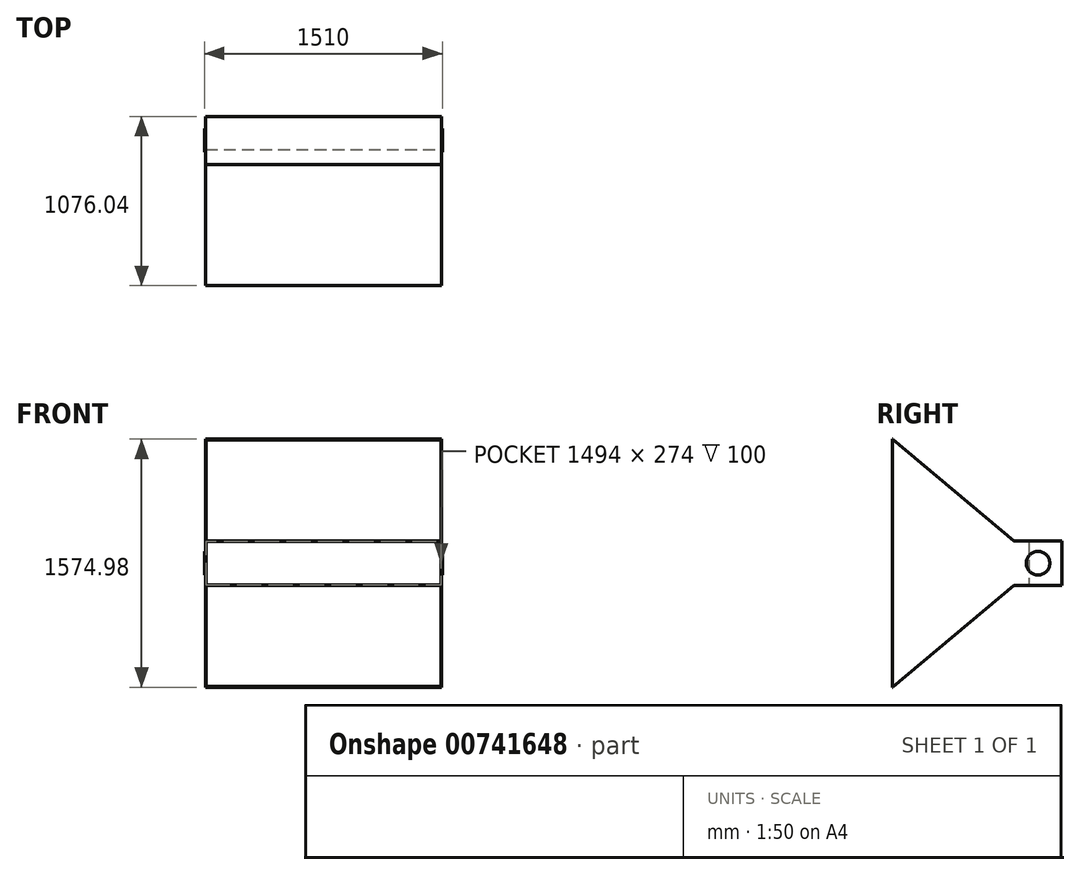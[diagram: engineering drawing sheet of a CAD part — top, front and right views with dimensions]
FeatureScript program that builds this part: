
annotation { "Feature Type Name" : "Feature", "Feature Type Description" : "" }
export const myFeature = defineFeature(function(context is Context, id is Id, definition is map)
    precondition{}
    {
        {
            var Q0;
            Q0=qCreatedBy(makeId("Front.planeOp"),FACE);
            var sketch = newSketch(context, id + "F0", { "sketchPlane" : qUnion([Q0])});
            skLineSegment(sketch, "E0.bottom", {"start": v(-750, 140) * mm, "end": v(750, 140) * mm});
            skLineSegment(sketch, "E0.top", {"start": v(-750, -140) * mm, "end": v(750, -140) * mm});
            skLineSegment(sketch, "E0.left", {"start": v(-750, 140) * mm, "end": v(-750, -140) * mm});
            skLineSegment(sketch, "E0.right", {"start": v(750, 140) * mm, "end": v(750, -140) * mm});
            skPoint(sketch, "E0.middle", {"position": v(0, 0) * mm});
            skSolve(sketch);
        }
        {
            var Q0;
            Q0=qSketchRegion(id+"F0",true);
            extrude(context, id + "F1", {"entities" : qUnion([Q0]), "oppositeDirection" : true, "depth" : 210 * mm});
        }
        {
            var Q0;
            Q0=makeQuery(id+"F1.opExtrude","CAP_FACE",FACE,{"disambiguationData":[OSD([sQuery(id+"F0.wireOp",EDGE,"E0.bottom"),sQuery(id+"F0.wireOp",EDGE,"E0.top"),sQuery(id+"F0.wireOp",EDGE,"E0.left"),sQuery(id+"F0.wireOp",EDGE,"E0.right")])],"isStart":true});
            var sketch = newSketch(context, id + "F2", { "sketchPlane" : qUnion([Q0])});
            skLineSegment(sketch, "E1.bottom", {"start": v(-750, 140) * mm, "end": v(750, 140) * mm});
            skLineSegment(sketch, "E1.top", {"start": v(-750, -140) * mm, "end": v(750, -140) * mm});
            skLineSegment(sketch, "E1.left", {"start": v(-750, 140) * mm, "end": v(-750, -140) * mm});
            skLineSegment(sketch, "E1.right", {"start": v(750, 140) * mm, "end": v(750, -140) * mm});
            skPoint(sketch, "E1.middle", {"position": v(0, 0) * mm});
            skLineSegment(sketch, "E2.bottom", {"start": v(-747, 137) * mm, "end": v(747, 137) * mm});
            skLineSegment(sketch, "E2.top", {"start": v(-747, -137) * mm, "end": v(747, -137) * mm});
            skLineSegment(sketch, "E2.left", {"start": v(-747, 137) * mm, "end": v(-747, -137) * mm});
            skLineSegment(sketch, "E2.right", {"start": v(747, 137) * mm, "end": v(747, -137) * mm});
            skSolve(sketch);
        }
        {
            var Q0;
            Q0=makeQuery(id+"F2.imprint","IMPRINT",FACE,{"disambiguationData":[TD([[makeQuery(id+"F2.imprint","IMPRINT",EDGE,{"derivedFrom":sQuery(id+"F2.wireOp",EDGE,"E1.bottom")}),-1.0]])]});
            extrude(context, id + "F3", {"entities" : qUnion([Q0]), "operationType" : NewBodyOperationType.ADD, "depth" : 100 * mm});
        }
        {
            var Q0;
            Q0=makeQuery(id+"F3.boolean.opBoolean","MERGE",FACE,{"derivedFrom":[makeQuery(id+"F1.opExtrude","SWEPT_FACE",FACE,{"disambiguationData":[OSD([sQuery(id+"F0.wireOp",EDGE,"E0.right")])]}),makeQuery(id+"F3.opExtrude","SWEPT_FACE",FACE,{"disambiguationData":[OSD([sQuery(id+"F2.wireOp",EDGE,"E1.right")])]})]});
            var sketch = newSketch(context, id + "F4", { "sketchPlane" : qUnion([Q0])});
            skLineSegment(sketch, "E3", {"start": v(-100, 140) * mm, "end": v(-866.04, 782.79) * mm});
            skLineSegment(sketch, "E4", {"start": v(-866.04, 782.79) * mm, "end": v(-866.04, 787.49) * mm});
            skLineSegment(sketch, "E5", {"start": v(-866.04, 787.49) * mm, "end": v(-863.44, 787.49) * mm});
            skLineSegment(sketch, "E6", {"start": v(-863.44, 787.49) * mm, "end": v(-863.44, 784.75) * mm});
            skLineSegment(sketch, "E7", {"start": v(-863.44, 784.75) * mm, "end": v(-95.06, 140) * mm});
            skLineSegment(sketch, "E8", {"start": v(0, 0) * mm, "end": v(-196.26, 0) * mm});
            skLineSegment(sketch, "E9.MirrorCS", {"start": v(-863.44, -784.75) * mm, "end": v(-95.06, -140) * mm});
            skLineSegment(sketch, "E10.MirrorCS", {"start": v(-866.04, -782.79) * mm, "end": v(-866.04, -787.49) * mm});
            skLineSegment(sketch, "E11.MirrorCS", {"start": v(-866.04, -787.49) * mm, "end": v(-863.44, -787.49) * mm});
            skLineSegment(sketch, "E12.MirrorCS", {"start": v(-863.44, -787.49) * mm, "end": v(-863.44, -784.75) * mm});
            skLineSegment(sketch, "E13.MirrorCS", {"start": v(-100, -140) * mm, "end": v(-866.04, -782.79) * mm});
            skSolve(sketch);
        }
        {
            var Q0;
            {var subQ0=sQuery(id+"F4.wireOp",EDGE,"E3");Q0=makeQuery(id+"F4.imprint","IMPRINT",FACE,{"disambiguationData":[TD([[makeQuery(id+"F4.imprint","IMPRINT",EDGE,{"derivedFrom":subQ0}),-1.0]])]});}
            var Q1;
            {var subQ0=sQuery(id+"F4.wireOp",EDGE,"E9.MirrorCS");Q1=makeQuery(id+"F4.imprint","IMPRINT",FACE,{"disambiguationData":[TD([[makeQuery(id+"F4.imprint","IMPRINT",EDGE,{"derivedFrom":subQ0}),1.0]])]});}
            extrude(context, id + "F5", {"entities" : qUnion([Q0, Q1]), "operationType" : NewBodyOperationType.ADD, "oppositeDirection" : true, "depth" : 1500 * mm});
        }
        {
            var Q0;
            {var subQ0=sQuery(id+"F2.wireOp",EDGE,"E1.right");var subQ1=sQuery(id+"F0.wireOp",EDGE,"E0.right");Q0=makeQuery(id+"F5.boolean.opBoolean","MERGE",FACE,{"derivedFrom":[makeQuery(id+"F3.boolean.opBoolean","MERGE",FACE,{"derivedFrom":[makeQuery(id+"F1.opExtrude","SWEPT_FACE",FACE,{"disambiguationData":[OSD([subQ1])]}),makeQuery(id+"F3.opExtrude","SWEPT_FACE",FACE,{"disambiguationData":[OSD([subQ0])]})]}),makeQuery(id+"F5.opExtrude","CAP_FACE",FACE,{"disambiguationData":[OSD([sQuery(id+"F0.wireOp",EDGE,"E0.bottom"),subQ1,sQuery(id+"F2.wireOp",EDGE,"E1.bottom"),subQ0,sQuery(id+"F4.wireOp",EDGE,"E3"),sQuery(id+"F4.wireOp",EDGE,"E4"),sQuery(id+"F4.wireOp",EDGE,"E5"),sQuery(id+"F4.wireOp",EDGE,"E6"),sQuery(id+"F4.wireOp",EDGE,"E7")])],"isStart":true}),makeQuery(id+"F5.opExtrude","CAP_FACE",FACE,{"disambiguationData":[OSD([sQuery(id+"F0.wireOp",EDGE,"E0.top"),subQ1,sQuery(id+"F2.wireOp",EDGE,"E1.top"),subQ0,sQuery(id+"F4.wireOp",EDGE,"E9.MirrorCS"),sQuery(id+"F4.wireOp",EDGE,"E10.MirrorCS"),sQuery(id+"F4.wireOp",EDGE,"E11.MirrorCS"),sQuery(id+"F4.wireOp",EDGE,"E12.MirrorCS"),sQuery(id+"F4.wireOp",EDGE,"E13.MirrorCS")])],"isStart":true})]});}
            var sketch = newSketch(context, id + "F6", { "sketchPlane" : qUnion([Q0])});
            skCircle(sketch, "E14", {"center": v(57.47, 0) * mm, "radius": 75 * mm});
            skPoint(sketch, "E14.centerSnap0", {"position": v(57.47, -140) * mm});
            skPoint(sketch, "E14.centerSnap1", {"position": v(-100, 0) * mm});
            skSolve(sketch);
        }
        {
            var Q0;
            Q0=qSketchRegion(id+"F6",true);
            var Q1;
            Q1=makeQuery(id+"F6.imprint","IMPRINT",FACE,{"disambiguationData":[TD([[makeQuery(id+"F6.imprint","IMPRINT",EDGE,{"derivedFrom":sQuery(id+"F6.wireOp",EDGE,"E14")}),1.0]])]});
            extrude(context, id + "F7", {"entities" : qUnion([Q0, Q1]), "operationType" : NewBodyOperationType.ADD, "depth" : 5 * mm});
        }
        {
            var Q0;
            {var subQ0=sQuery(id+"F2.wireOp",EDGE,"E1.right");var subQ1=sQuery(id+"F0.wireOp",EDGE,"E0.right");Q0=makeQuery(id+"F5.boolean.opBoolean","MERGE",FACE,{"derivedFrom":[makeQuery(id+"F3.boolean.opBoolean","MERGE",FACE,{"derivedFrom":[makeQuery(id+"F1.opExtrude","SWEPT_FACE",FACE,{"disambiguationData":[OSD([sQuery(id+"F0.wireOp",EDGE,"E0.left")])]}),makeQuery(id+"F3.opExtrude","SWEPT_FACE",FACE,{"disambiguationData":[OSD([sQuery(id+"F2.wireOp",EDGE,"E1.left")])]})]}),makeQuery(id+"F5.opExtrude","CAP_FACE",FACE,{"disambiguationData":[OSD([sQuery(id+"F0.wireOp",EDGE,"E0.bottom"),subQ1,sQuery(id+"F2.wireOp",EDGE,"E1.bottom"),subQ0,sQuery(id+"F4.wireOp",EDGE,"E3"),sQuery(id+"F4.wireOp",EDGE,"E4"),sQuery(id+"F4.wireOp",EDGE,"E5"),sQuery(id+"F4.wireOp",EDGE,"E6"),sQuery(id+"F4.wireOp",EDGE,"E7")])],"isStart":false}),makeQuery(id+"F5.opExtrude","CAP_FACE",FACE,{"disambiguationData":[OSD([sQuery(id+"F0.wireOp",EDGE,"E0.top"),subQ1,sQuery(id+"F2.wireOp",EDGE,"E1.top"),subQ0,sQuery(id+"F4.wireOp",EDGE,"E9.MirrorCS"),sQuery(id+"F4.wireOp",EDGE,"E10.MirrorCS"),sQuery(id+"F4.wireOp",EDGE,"E11.MirrorCS"),sQuery(id+"F4.wireOp",EDGE,"E12.MirrorCS"),sQuery(id+"F4.wireOp",EDGE,"E13.MirrorCS")])],"isStart":false})]});}
            var sketch = newSketch(context, id + "F8", { "sketchPlane" : qUnion([Q0])});
            skCircle(sketch, "E15", {"center": v(-57.47, 0) * mm, "radius": 75 * mm});
            skPoint(sketch, "E15.centerSnap0", {"position": v(-57.47, 140) * mm});
            skPoint(sketch, "E15.centerSnap1", {"position": v(100, 0) * mm});
            skSolve(sketch);
        }
        {
            var Q0;
            Q0=qSketchRegion(id+"F8",true);
            extrude(context, id + "F9", {"entities" : qUnion([Q0]), "operationType" : NewBodyOperationType.ADD, "depth" : 5 * mm});
        }
        {
            var Q0;
            {var subQ0=sQuery(id+"F2.wireOp",EDGE,"E1.right");var subQ1=sQuery(id+"F0.wireOp",EDGE,"E0.right");Q0=makeQuery(id+"F5.boolean.opBoolean","MERGE",FACE,{"derivedFrom":[makeQuery(id+"F3.boolean.opBoolean","MERGE",FACE,{"derivedFrom":[makeQuery(id+"F1.opExtrude","SWEPT_FACE",FACE,{"disambiguationData":[OSD([sQuery(id+"F0.wireOp",EDGE,"E0.left")])]}),makeQuery(id+"F3.opExtrude","SWEPT_FACE",FACE,{"disambiguationData":[OSD([sQuery(id+"F2.wireOp",EDGE,"E1.left")])]})]}),makeQuery(id+"F5.opExtrude","CAP_FACE",FACE,{"disambiguationData":[OSD([sQuery(id+"F0.wireOp",EDGE,"E0.bottom"),subQ1,sQuery(id+"F2.wireOp",EDGE,"E1.bottom"),subQ0,sQuery(id+"F4.wireOp",EDGE,"E3"),sQuery(id+"F4.wireOp",EDGE,"E4"),sQuery(id+"F4.wireOp",EDGE,"E5"),sQuery(id+"F4.wireOp",EDGE,"E6"),sQuery(id+"F4.wireOp",EDGE,"E7")])],"isStart":false}),makeQuery(id+"F5.opExtrude","CAP_FACE",FACE,{"disambiguationData":[OSD([sQuery(id+"F0.wireOp",EDGE,"E0.top"),subQ1,sQuery(id+"F2.wireOp",EDGE,"E1.top"),subQ0,sQuery(id+"F4.wireOp",EDGE,"E9.MirrorCS"),sQuery(id+"F4.wireOp",EDGE,"E10.MirrorCS"),sQuery(id+"F4.wireOp",EDGE,"E11.MirrorCS"),sQuery(id+"F4.wireOp",EDGE,"E12.MirrorCS"),sQuery(id+"F4.wireOp",EDGE,"E13.MirrorCS")])],"isStart":false})]});}
            var sketch = newSketch(context, id + "F10", { "sketchPlane" : qUnion([Q0])});
            skLineSegment(sketch, "E16", {"start": v(863.44, 787.49) * mm, "end": v(866.04, 787.49) * mm});
            skLineSegment(sketch, "E17", {"start": v(866.04, 787.49) * mm, "end": v(866.04, 782.79) * mm});
            skLineSegment(sketch, "E18", {"start": v(866.04, 782.79) * mm, "end": v(866.04, -782.79) * mm});
            skLineSegment(sketch, "E19", {"start": v(866.04, -782.79) * mm, "end": v(866.04, -787.49) * mm});
            skLineSegment(sketch, "E20", {"start": v(866.04, -787.49) * mm, "end": v(863.44, -787.49) * mm});
            skLineSegment(sketch, "E21", {"start": v(863.44, -787.49) * mm, "end": v(863.44, -784.75) * mm});
            skLineSegment(sketch, "E22", {"start": v(863.44, -784.75) * mm, "end": v(95.06, -140) * mm});
            skLineSegment(sketch, "E23", {"start": v(95.06, -140) * mm, "end": v(100, -140) * mm});
            skLineSegment(sketch, "E24", {"start": v(100, -140) * mm, "end": v(100, 140) * mm});
            skLineSegment(sketch, "E25", {"start": v(100, 140) * mm, "end": v(95.06, 140) * mm});
            skLineSegment(sketch, "E26", {"start": v(95.06, 140) * mm, "end": v(863.44, 784.75) * mm});
            skLineSegment(sketch, "E27", {"start": v(863.44, 784.75) * mm, "end": v(863.44, 787.49) * mm});
            skSolve(sketch);
        }
        {
            var Q0;
            Q0=makeQuery(id+"F10.imprint","IMPRINT",FACE,{"disambiguationData":[TD([[makeQuery(id+"F10.imprint","IMPRINT",EDGE,{"derivedFrom":sQuery(id+"F10.wireOp",EDGE,"E18")}),-1.0]])]});
            var Q1;
            Q1=makeQuery(id+"F10.imprint","IMPRINT",FACE,{"disambiguationData":[TD([[makeQuery(id+"F10.imprint","IMPRINT",EDGE,{"derivedFrom":sQuery(id+"F10.wireOp",EDGE,"E16")}),1.0]])]});
            var Q2;
            Q2=makeQuery(id+"F10.imprint","IMPRINT",FACE,{"disambiguationData":[TD([[makeQuery(id+"F10.imprint","IMPRINT",EDGE,{"derivedFrom":sQuery(id+"F10.wireOp",EDGE,"E19")}),-1.0]])]});
            extrude(context, id + "F11", {"entities" : qUnion([Q0, Q1, Q2]), "operationType" : NewBodyOperationType.ADD, "oppositeDirection" : true, "depth" : 3 * mm});
        }
        {
            var Q0;
            {var subQ0=sQuery(id+"F2.wireOp",EDGE,"E1.right");var subQ1=sQuery(id+"F0.wireOp",EDGE,"E0.right");Q0=makeQuery(id+"F5.boolean.opBoolean","MERGE",FACE,{"derivedFrom":[makeQuery(id+"F3.boolean.opBoolean","MERGE",FACE,{"derivedFrom":[makeQuery(id+"F1.opExtrude","SWEPT_FACE",FACE,{"disambiguationData":[OSD([subQ1])]}),makeQuery(id+"F3.opExtrude","SWEPT_FACE",FACE,{"disambiguationData":[OSD([subQ0])]})]}),makeQuery(id+"F5.opExtrude","CAP_FACE",FACE,{"disambiguationData":[OSD([sQuery(id+"F0.wireOp",EDGE,"E0.bottom"),subQ1,sQuery(id+"F2.wireOp",EDGE,"E1.bottom"),subQ0,sQuery(id+"F4.wireOp",EDGE,"E3"),sQuery(id+"F4.wireOp",EDGE,"E4"),sQuery(id+"F4.wireOp",EDGE,"E5"),sQuery(id+"F4.wireOp",EDGE,"E6"),sQuery(id+"F4.wireOp",EDGE,"E7")])],"isStart":true}),makeQuery(id+"F5.opExtrude","CAP_FACE",FACE,{"disambiguationData":[OSD([sQuery(id+"F0.wireOp",EDGE,"E0.top"),subQ1,sQuery(id+"F2.wireOp",EDGE,"E1.top"),subQ0,sQuery(id+"F4.wireOp",EDGE,"E9.MirrorCS"),sQuery(id+"F4.wireOp",EDGE,"E10.MirrorCS"),sQuery(id+"F4.wireOp",EDGE,"E11.MirrorCS"),sQuery(id+"F4.wireOp",EDGE,"E12.MirrorCS"),sQuery(id+"F4.wireOp",EDGE,"E13.MirrorCS")])],"isStart":true})]});}
            var sketch = newSketch(context, id + "F12", { "sketchPlane" : qUnion([Q0])});
            skLineSegment(sketch, "E28", {"start": v(-866.04, -787.49) * mm, "end": v(-863.44, -787.49) * mm});
            skLineSegment(sketch, "E29", {"start": v(-863.44, -787.49) * mm, "end": v(-863.44, -784.75) * mm});
            skLineSegment(sketch, "E30", {"start": v(-863.44, -784.75) * mm, "end": v(-95.06, -140) * mm});
            skLineSegment(sketch, "E31", {"start": v(-95.06, -140) * mm, "end": v(-100, -140) * mm});
            skLineSegment(sketch, "E32", {"start": v(-100, -140) * mm, "end": v(-100, 140) * mm});
            skLineSegment(sketch, "E33", {"start": v(-100, 140) * mm, "end": v(-95.06, 140) * mm});
            skLineSegment(sketch, "E34", {"start": v(-95.06, 140) * mm, "end": v(-863.44, 784.75) * mm});
            skLineSegment(sketch, "E35", {"start": v(-863.44, 784.75) * mm, "end": v(-863.44, 787.49) * mm});
            skLineSegment(sketch, "E36", {"start": v(-863.44, 787.49) * mm, "end": v(-866.04, 787.49) * mm});
            skLineSegment(sketch, "E37", {"start": v(-866.04, 787.49) * mm, "end": v(-866.04, 782.79) * mm});
            skLineSegment(sketch, "E38", {"start": v(-866.04, 782.79) * mm, "end": v(-866.04, -782.79) * mm});
            skLineSegment(sketch, "E39", {"start": v(-866.04, -782.79) * mm, "end": v(-866.04, -787.49) * mm});
            skSolve(sketch);
        }
        {
            var Q0;
            Q0=makeQuery(id+"F12.imprint","IMPRINT",FACE,{"disambiguationData":[TD([[makeQuery(id+"F12.imprint","IMPRINT",EDGE,{"derivedFrom":sQuery(id+"F12.wireOp",EDGE,"E32")}),-1.0]])]});
            var Q1;
            Q1=makeQuery(id+"F12.imprint","IMPRINT",FACE,{"disambiguationData":[TD([[makeQuery(id+"F12.imprint","IMPRINT",EDGE,{"derivedFrom":sQuery(id+"F12.wireOp",EDGE,"E28")}),1.0]])]});
            extrude(context, id + "F13", {"entities" : qUnion([Q0, Q1]), "operationType" : NewBodyOperationType.ADD, "oppositeDirection" : true, "depth" : 3 * mm});
        }
    });
